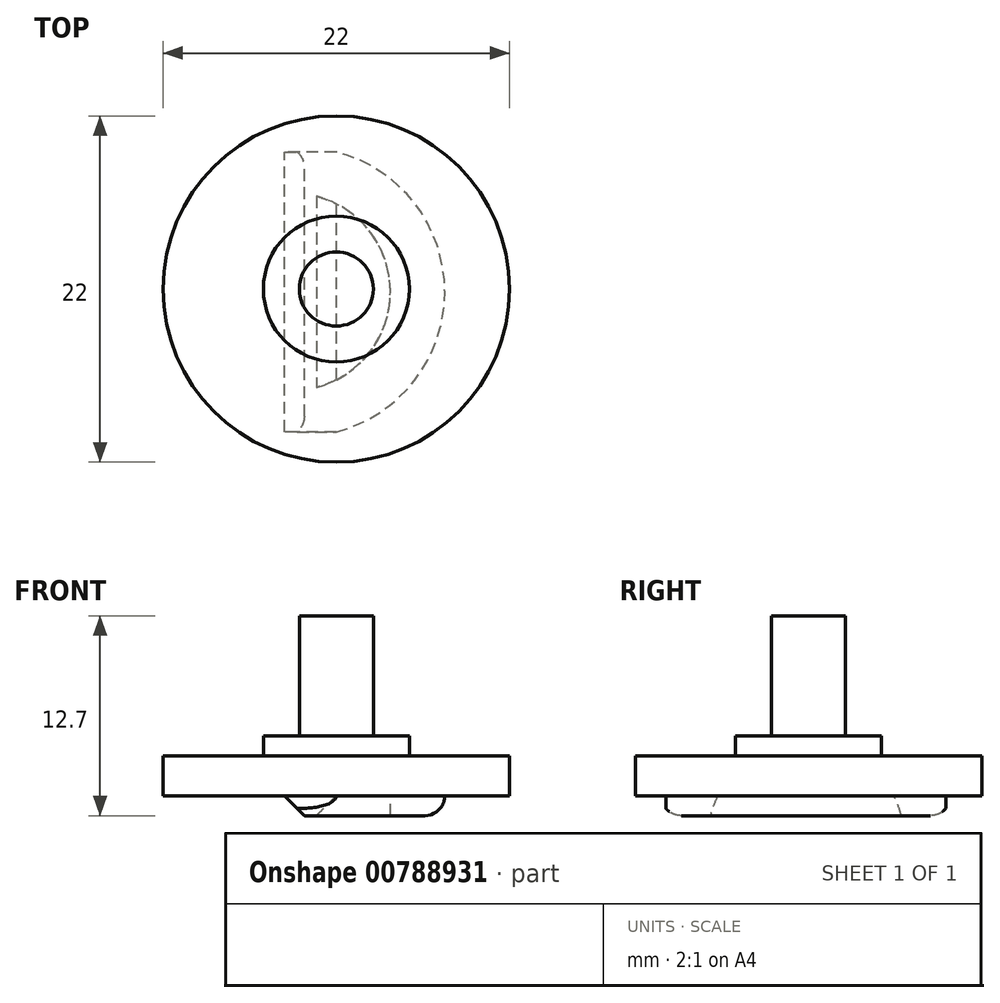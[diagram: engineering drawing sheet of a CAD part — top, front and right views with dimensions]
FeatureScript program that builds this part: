
annotation { "Feature Type Name" : "Feature", "Feature Type Description" : "" }
export const myFeature = defineFeature(function(context is Context, id is Id, definition is map)
    precondition{}
    {
        {
            var Q0;
            Q0=qCreatedBy(makeId("Top.planeOp"),FACE);
            var sketch = newSketch(context, id + "F0", { "sketchPlane" : qUnion([Q0])});
            skCircle(sketch, "E0", {"center": v(0, 0) * mm, "radius": 11 * mm});
            skCircle(sketch, "E1", {"center": v(0, 0) * mm, "radius": 4.64 * mm});
            skCircle(sketch, "E2", {"center": v(0, 0) * mm, "radius": 2.35 * mm});
            skSolve(sketch);
        }
        {
            var Q0;
            Q0=makeQuery(id+"F0.imprint","IMPRINT",FACE,{"disambiguationData":[TD([[makeQuery(id+"F0.imprint","IMPRINT",EDGE,{"derivedFrom":sQuery(id+"F0.wireOp",EDGE,"E2")}),1.0]])]});
            extrude(context, id + "F1", {"entities" : qUnion([Q0]), "depth" : 11.43 * mm, "offsetDistance" : 25.4 * mm});
        }
        {
            var Q0;
            Q0=makeQuery(id+"F0.imprint","IMPRINT",FACE,{"disambiguationData":[TD([[makeQuery(id+"F0.imprint","IMPRINT",EDGE,{"derivedFrom":sQuery(id+"F0.wireOp",EDGE,"E1")}),1.0]])]});
            extrude(context, id + "F2", {"entities" : qUnion([Q0]), "operationType" : NewBodyOperationType.ADD, "depth" : 3.8 * mm, "offsetDistance" : 25.4 * mm});
        }
        {
            var Q0;
            Q0=makeQuery(id+"F0.imprint","IMPRINT",FACE,{"disambiguationData":[TD([[makeQuery(id+"F0.imprint","IMPRINT",EDGE,{"derivedFrom":sQuery(id+"F0.wireOp",EDGE,"E0")}),1.0]])]});
            extrude(context, id + "F3", {"entities" : qUnion([Q0]), "operationType" : NewBodyOperationType.ADD, "depth" : 2.54 * mm, "offsetDistance" : 25.4 * mm});
        }
        {
            var Q0;
            Q0=makeQuery(id+"F0.imprint","IMPRINT",FACE,{"disambiguationData":[TD([[makeQuery(id+"F0.imprint","IMPRINT",EDGE,{"derivedFrom":sQuery(id+"F0.wireOp",EDGE,"E0")}),1.0]])]});
            var sketch = newSketch(context, id + "F4", { "sketchPlane" : qUnion([Q0])});
            skArc(sketch, "E3", {"start": v(0, -5.76) * mm, "mid": v(3.43, -0.18) * mm, "end": v(0, 5.41) * mm});
            skArc(sketch, "E4", {"start": v(0, -9.07) * mm, "mid": v(6.9, -0.18) * mm, "end": v(0, 8.71) * mm});
            skLineSegment(sketch, "E5.bottom", {"start": v(0, -9.07) * mm, "end": v(-3.3, -9.07) * mm});
            skLineSegment(sketch, "E5.top", {"start": v(0, 8.71) * mm, "end": v(-3.3, 8.71) * mm});
            skLineSegment(sketch, "E5.left", {"start": v(0, -9.07) * mm, "end": v(0, 8.71) * mm});
            skLineSegment(sketch, "E5.right", {"start": v(-3.3, -9.07) * mm, "end": v(-3.3, 8.71) * mm});
            skSolve(sketch);
        }
        {
            var Q0;
            Q0 = qSketchRegion(id + "F4", true);
            extrude(context, id + "F5", {"entities" : qUnion([Q0]), "operationType" : NewBodyOperationType.ADD, "oppositeDirection" : true, "depth" : 1.27 * mm, "offsetDistance" : 25.4 * mm});
        }
        {
            var Q0;
            Q0=makeQuery(id+"F5.opExtrude","CAP_EDGE",EDGE,{"disambiguationData":[OSD([sQuery(id+"F4.wireOp",EDGE,"E5.right")])],"isStart":false});
            var Q1;
            Q1=makeQuery(id+"F5.opExtrude","CAP_EDGE",EDGE,{"disambiguationData":[OSD([sQuery(id+"F4.wireOp",EDGE,"E5.left")])],"isStart":false});
            chamfer(context, id + "F6", {"entities" : qUnion([Q0, Q1]), "width" : 1.27 * mm, "tangentPropagation" : true});
        }
        {
            var Q0;
            Q0=makeQuery(id+"F5.opExtrude","CAP_EDGE",EDGE,{"disambiguationData":[OSD([sQuery(id+"F4.wireOp",EDGE,"E4")])],"isStart":false});
            fillet(context, id + "F7", {"entities" : qUnion([Q0]), "radius" : 1.27 * mm, "tangentPropagation" : true, "allowEdgeOverflow" : false});
        }
    });
